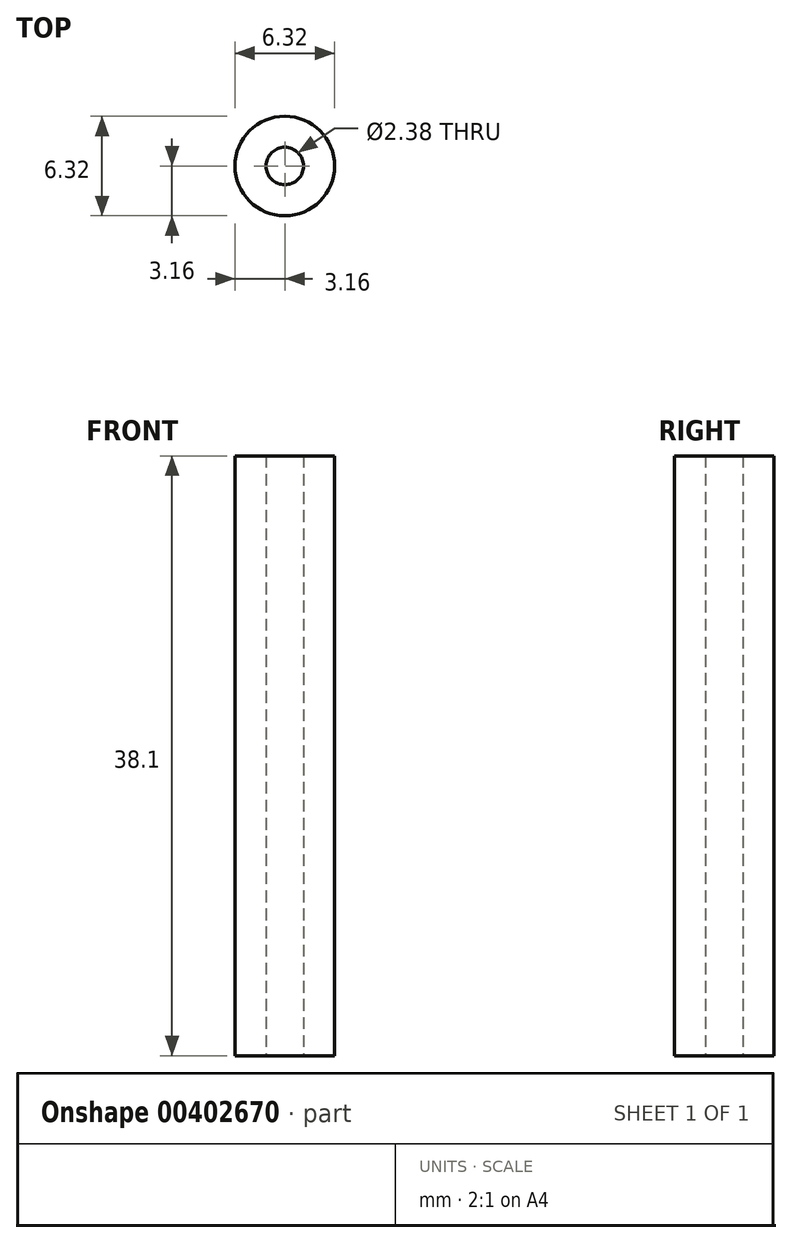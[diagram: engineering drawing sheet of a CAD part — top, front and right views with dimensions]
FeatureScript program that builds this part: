
annotation { "Feature Type Name" : "Feature", "Feature Type Description" : "" }
export const myFeature = defineFeature(function(context is Context, id is Id, definition is map)
    precondition{}
    {
        {
            var Q0;
            Q0=qCreatedBy(makeId("Top.planeOp"),FACE);
            var sketch = newSketch(context, id + "F0", { "sketchPlane" : qUnion([Q0])});
            skCircle(sketch, "E0", {"center": v(0, 0) * mm, "radius": 3.16 * mm});
            skCircle(sketch, "E1", {"center": v(0, 0) * mm, "radius": 1.2 * mm});
            skSolve(sketch);
        }
        {
            var Q0;
            Q0 = qSketchRegion(id + "F0", true);
            extrude(context, id + "F1", {"entities" : qUnion([Q0]), "endBound" : BoundingType.SYMMETRIC, "depth" : 38.1 * mm});
        }
    });
